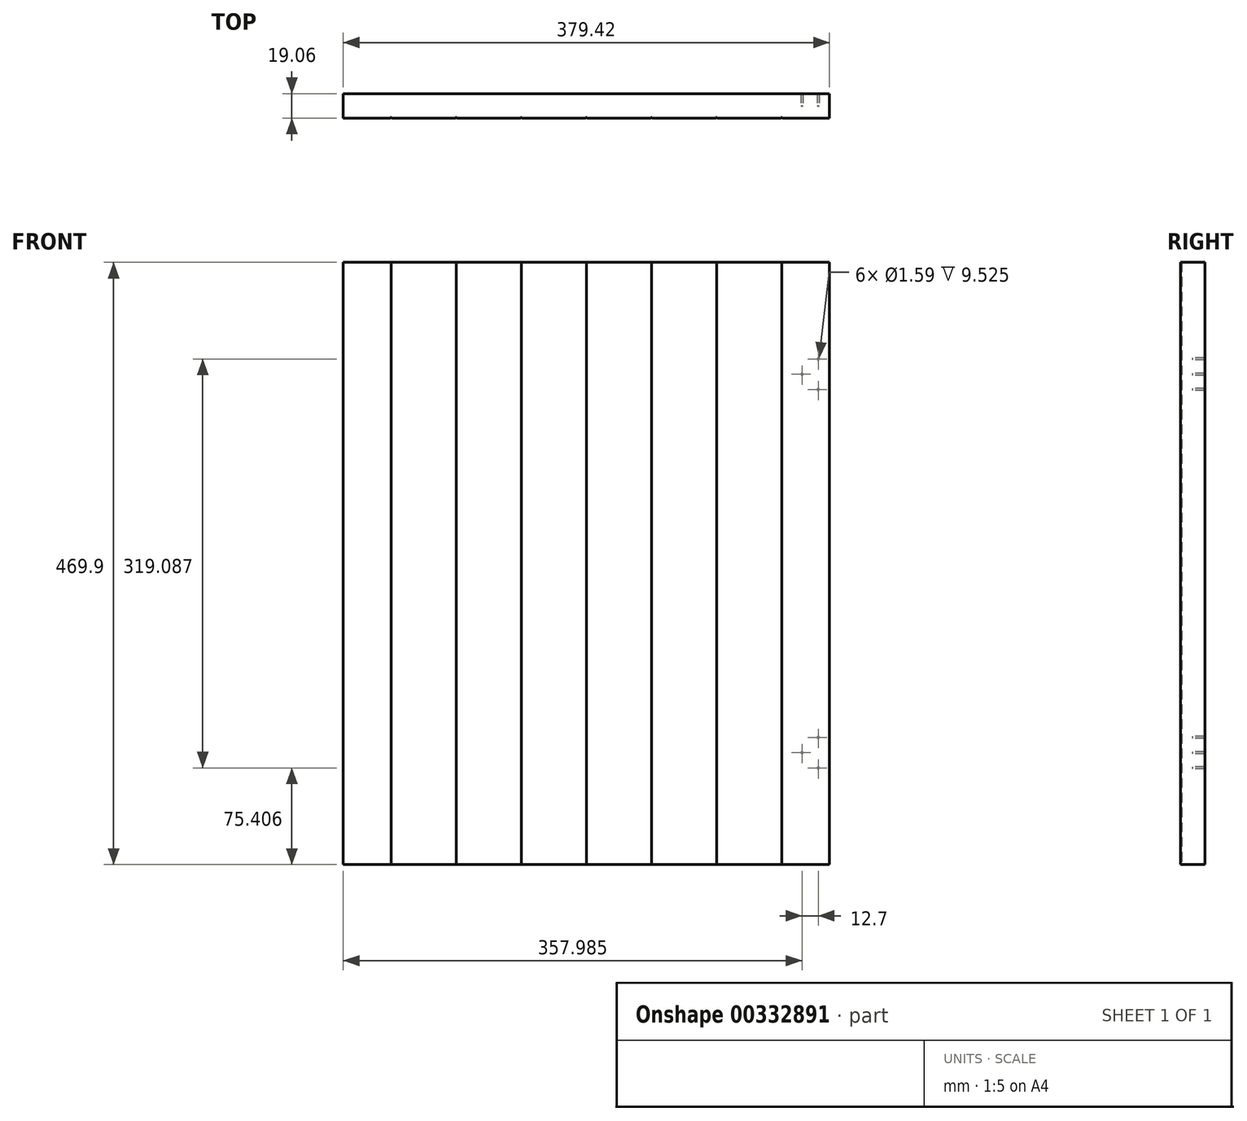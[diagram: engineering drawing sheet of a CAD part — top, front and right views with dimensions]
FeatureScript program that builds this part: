
annotation { "Feature Type Name" : "Feature", "Feature Type Description" : "" }
export const myFeature = defineFeature(function(context is Context, id is Id, definition is map)
    precondition{}
    {
        {
            var Q0;
            Q0=qCreatedBy(makeId("Top.planeOp"),FACE);
            var sketch = newSketch(context, id + "F0", { "sketchPlane" : qUnion([Q0])});
            skLineSegment(sketch, "E0.bottom", {"start": v(508, -9.53) * mm, "end": v(458.22, -9.53) * mm});
            skLineSegment(sketch, "E0.top", {"start": v(508, 9.53) * mm, "end": v(-508, 9.53) * mm});
            skLineSegment(sketch, "E0.left", {"start": v(508, 9.53) * mm, "end": v(508, -9.53) * mm});
            skLineSegment(sketch, "E0.right", {"start": v(-508, 9.53) * mm, "end": v(-508, -9.53) * mm});
            skPoint(sketch, "E0.middle", {"position": v(0, 0) * mm});
            skArc(sketch, "E1", {"start": v(-509.02, -9.53) * mm, "mid": v(-508.3, -9.23) * mm, "end": v(-508, -8.5) * mm});
            skArc(sketch, "E2", {"start": v(-508, -8.5) * mm, "mid": v(-507.7, -9.23) * mm, "end": v(-506.98, -9.52) * mm});
            skArc(sketch, "E3.1.0.0", {"start": v(-458.22, -9.53) * mm, "mid": v(-457.5, -9.23) * mm, "end": v(-457.2, -8.5) * mm});
            skArc(sketch, "E3.1.0.1", {"start": v(-457.2, -8.5) * mm, "mid": v(-456.9, -9.23) * mm, "end": v(-456.18, -9.52) * mm});
            skArc(sketch, "E3.2.0.0", {"start": v(-407.42, -9.53) * mm, "mid": v(-406.7, -9.23) * mm, "end": v(-406.4, -8.5) * mm});
            skArc(sketch, "E3.2.0.1", {"start": v(-406.4, -8.5) * mm, "mid": v(-406.1, -9.23) * mm, "end": v(-405.38, -9.52) * mm});
            skArc(sketch, "E3.3.0.0", {"start": v(-356.62, -9.53) * mm, "mid": v(-355.9, -9.23) * mm, "end": v(-355.6, -8.5) * mm});
            skArc(sketch, "E3.3.0.1", {"start": v(-355.6, -8.5) * mm, "mid": v(-355.3, -9.23) * mm, "end": v(-354.58, -9.52) * mm});
            skArc(sketch, "E3.4.0.0", {"start": v(-305.82, -9.53) * mm, "mid": v(-305.1, -9.23) * mm, "end": v(-304.8, -8.5) * mm});
            skArc(sketch, "E3.4.0.1", {"start": v(-304.8, -8.5) * mm, "mid": v(-304.5, -9.23) * mm, "end": v(-303.78, -9.52) * mm});
            skArc(sketch, "E3.5.0.0", {"start": v(-255.02, -9.53) * mm, "mid": v(-254.3, -9.23) * mm, "end": v(-254, -8.5) * mm});
            skArc(sketch, "E3.5.0.1", {"start": v(-254, -8.5) * mm, "mid": v(-253.7, -9.23) * mm, "end": v(-252.98, -9.52) * mm});
            skArc(sketch, "E3.6.0.0", {"start": v(-204.22, -9.53) * mm, "mid": v(-203.5, -9.23) * mm, "end": v(-203.2, -8.5) * mm});
            skArc(sketch, "E3.6.0.1", {"start": v(-203.2, -8.5) * mm, "mid": v(-202.9, -9.23) * mm, "end": v(-202.18, -9.52) * mm});
            skArc(sketch, "E3.7.0.0", {"start": v(-153.42, -9.53) * mm, "mid": v(-152.7, -9.23) * mm, "end": v(-152.4, -8.5) * mm});
            skArc(sketch, "E3.7.0.1", {"start": v(-152.4, -8.5) * mm, "mid": v(-152.1, -9.23) * mm, "end": v(-151.38, -9.52) * mm});
            skArc(sketch, "E3.8.0.0", {"start": v(-102.62, -9.53) * mm, "mid": v(-101.9, -9.23) * mm, "end": v(-101.6, -8.5) * mm});
            skArc(sketch, "E3.8.0.1", {"start": v(-101.6, -8.5) * mm, "mid": v(-101.3, -9.23) * mm, "end": v(-100.58, -9.52) * mm});
            skArc(sketch, "E3.9.0.0", {"start": v(-51.82, -9.53) * mm, "mid": v(-51.1, -9.23) * mm, "end": v(-50.8, -8.5) * mm});
            skArc(sketch, "E3.9.0.1", {"start": v(-50.8, -8.5) * mm, "mid": v(-50.5, -9.23) * mm, "end": v(-49.78, -9.52) * mm});
            skArc(sketch, "E3.10.0.0", {"start": v(-1.02, -9.53) * mm, "mid": v(-0.3, -9.23) * mm, "end": v(0, -8.5) * mm});
            skArc(sketch, "E3.10.0.1", {"start": v(0, -8.5) * mm, "mid": v(0.3, -9.23) * mm, "end": v(1.02, -9.52) * mm});
            skArc(sketch, "E3.11.0.0", {"start": v(49.78, -9.53) * mm, "mid": v(50.5, -9.23) * mm, "end": v(50.8, -8.5) * mm});
            skArc(sketch, "E3.11.0.1", {"start": v(50.8, -8.5) * mm, "mid": v(51.1, -9.23) * mm, "end": v(51.82, -9.52) * mm});
            skArc(sketch, "E3.12.0.0", {"start": v(100.58, -9.53) * mm, "mid": v(101.3, -9.23) * mm, "end": v(101.6, -8.5) * mm});
            skArc(sketch, "E3.12.0.1", {"start": v(101.6, -8.5) * mm, "mid": v(101.9, -9.23) * mm, "end": v(102.62, -9.52) * mm});
            skArc(sketch, "E3.13.0.0", {"start": v(151.38, -9.53) * mm, "mid": v(152.1, -9.23) * mm, "end": v(152.4, -8.5) * mm});
            skArc(sketch, "E3.13.0.1", {"start": v(152.4, -8.5) * mm, "mid": v(152.7, -9.23) * mm, "end": v(153.42, -9.52) * mm});
            skArc(sketch, "E3.14.0.0", {"start": v(202.18, -9.53) * mm, "mid": v(202.9, -9.23) * mm, "end": v(203.2, -8.5) * mm});
            skArc(sketch, "E3.14.0.1", {"start": v(203.2, -8.5) * mm, "mid": v(203.5, -9.23) * mm, "end": v(204.22, -9.52) * mm});
            skArc(sketch, "E3.15.0.0", {"start": v(252.98, -9.53) * mm, "mid": v(253.7, -9.23) * mm, "end": v(254, -8.5) * mm});
            skArc(sketch, "E3.15.0.1", {"start": v(254, -8.5) * mm, "mid": v(254.3, -9.23) * mm, "end": v(255.02, -9.52) * mm});
            skArc(sketch, "E3.16.0.0", {"start": v(303.78, -9.53) * mm, "mid": v(304.5, -9.23) * mm, "end": v(304.8, -8.5) * mm});
            skArc(sketch, "E3.16.0.1", {"start": v(304.8, -8.5) * mm, "mid": v(305.1, -9.23) * mm, "end": v(305.82, -9.52) * mm});
            skArc(sketch, "E3.17.0.0", {"start": v(354.58, -9.53) * mm, "mid": v(355.3, -9.23) * mm, "end": v(355.6, -8.5) * mm});
            skArc(sketch, "E3.17.0.1", {"start": v(355.6, -8.5) * mm, "mid": v(355.9, -9.23) * mm, "end": v(356.62, -9.52) * mm});
            skArc(sketch, "E3.18.0.0", {"start": v(405.38, -9.53) * mm, "mid": v(406.1, -9.23) * mm, "end": v(406.4, -8.5) * mm});
            skArc(sketch, "E3.18.0.1", {"start": v(406.4, -8.5) * mm, "mid": v(406.7, -9.23) * mm, "end": v(407.42, -9.52) * mm});
            skArc(sketch, "E3.19.0.0", {"start": v(456.18, -9.53) * mm, "mid": v(456.9, -9.23) * mm, "end": v(457.2, -8.5) * mm});
            skArc(sketch, "E3.19.0.1", {"start": v(457.2, -8.5) * mm, "mid": v(457.5, -9.23) * mm, "end": v(458.22, -9.52) * mm});
            skLineSegment(sketch, "E3.direction1", {"start": v(-506.98, -9.53) * mm, "end": v(-458.22, -9.53) * mm, "construction": true});
            skLineSegment(sketch, "E4.trimOffspring", {"start": v(-458.22, -9.53) * mm, "end": v(-508, -9.53) * mm});
            skLineSegment(sketch, "E5.trimOffspring", {"start": v(-407.42, -9.53) * mm, "end": v(-456.18, -9.53) * mm});
            skLineSegment(sketch, "E6.trimOffspring", {"start": v(-356.62, -9.53) * mm, "end": v(-405.38, -9.53) * mm});
            skLineSegment(sketch, "E7.trimOffspring", {"start": v(-305.82, -9.53) * mm, "end": v(-354.58, -9.53) * mm});
            skLineSegment(sketch, "E8.trimOffspring", {"start": v(-255.02, -9.53) * mm, "end": v(-303.78, -9.53) * mm});
            skLineSegment(sketch, "E9.trimOffspring", {"start": v(-204.22, -9.53) * mm, "end": v(-252.98, -9.53) * mm});
            skLineSegment(sketch, "E10.trimOffspring", {"start": v(-153.42, -9.53) * mm, "end": v(-202.18, -9.53) * mm});
            skLineSegment(sketch, "E11.trimOffspring", {"start": v(-102.62, -9.53) * mm, "end": v(-151.38, -9.53) * mm});
            skLineSegment(sketch, "E12.trimOffspring", {"start": v(-51.82, -9.53) * mm, "end": v(-100.58, -9.53) * mm});
            skLineSegment(sketch, "E13.trimOffspring", {"start": v(-1.02, -9.53) * mm, "end": v(-49.78, -9.53) * mm});
            skLineSegment(sketch, "E14.trimOffspring", {"start": v(49.78, -9.53) * mm, "end": v(1.02, -9.53) * mm});
            skLineSegment(sketch, "E15.trimOffspring", {"start": v(100.58, -9.53) * mm, "end": v(51.82, -9.53) * mm});
            skLineSegment(sketch, "E16.trimOffspring", {"start": v(151.38, -9.53) * mm, "end": v(102.62, -9.53) * mm});
            skLineSegment(sketch, "E17.trimOffspring", {"start": v(202.18, -9.53) * mm, "end": v(153.42, -9.53) * mm});
            skLineSegment(sketch, "E18.trimOffspring", {"start": v(252.98, -9.53) * mm, "end": v(204.22, -9.53) * mm});
            skLineSegment(sketch, "E19.trimOffspring", {"start": v(303.78, -9.53) * mm, "end": v(255.02, -9.53) * mm});
            skLineSegment(sketch, "E20.trimOffspring", {"start": v(354.58, -9.53) * mm, "end": v(305.82, -9.53) * mm});
            skLineSegment(sketch, "E21.trimOffspring", {"start": v(405.38, -9.53) * mm, "end": v(356.62, -9.53) * mm});
            skLineSegment(sketch, "E22.trimOffspring", {"start": v(456.18, -9.53) * mm, "end": v(407.42, -9.53) * mm});
            skSolve(sketch);
        }
        {
            var Q0;
            Q0=qSketchRegion(id+"F0",true);
            extrude(context, id + "F1", {"entities" : qUnion([Q0]), "depth" : 469.9 * mm});
        }
        {
            var Q0;
            Q0=qCreatedBy(makeId("Top.planeOp"),FACE);
            var sketch = newSketch(context, id + "F2", { "sketchPlane" : qUnion([Q0])});
            skLineSegment(sketch, "E23.bottom", {"start": v(189.7, -89.59) * mm, "end": v(532.78, -89.59) * mm});
            skLineSegment(sketch, "E23.top", {"start": v(189.7, 47.64) * mm, "end": v(532.78, 47.64) * mm});
            skLineSegment(sketch, "E23.left", {"start": v(189.7, -89.59) * mm, "end": v(189.7, 47.64) * mm});
            skLineSegment(sketch, "E23.right", {"start": v(532.78, -89.59) * mm, "end": v(532.78, 47.64) * mm});
            skLineSegment(sketch, "E24.bottom", {"start": v(-189.7, -137.09) * mm, "end": v(-570.7, -137.09) * mm});
            skLineSegment(sketch, "E24.top", {"start": v(-189.7, 58.2) * mm, "end": v(-570.7, 58.2) * mm});
            skLineSegment(sketch, "E24.left", {"start": v(-189.7, -137.09) * mm, "end": v(-189.7, 58.2) * mm});
            skLineSegment(sketch, "E24.right", {"start": v(-570.7, -137.09) * mm, "end": v(-570.7, 58.2) * mm});
            skSolve(sketch);
        }
        {
            var Q0;
            Q0=qSketchRegion(id+"F2",true);
            extrude(context, id + "F3", {"entities" : qUnion([Q0]), "operationType" : NewBodyOperationType.REMOVE, "depth" : 1143 * mm});
        }
        {
            var Q0;
            Q0=qCreatedBy(makeId("Front.planeOp"),FACE);
            var sketch = newSketch(context, id + "F4", { "sketchPlane" : qUnion([Q0])});
            skPoint(sketch, "E25.middle", {"position": v(0, 454.03) * mm});
            skLineSegment(sketch, "E26.bottom", {"start": v(168.28, 0) * mm, "end": v(180.98, 0) * mm, "construction": true});
            skLineSegment(sketch, "E26.top", {"start": v(168.28, 469.9) * mm, "end": v(180.97, 469.9) * mm, "construction": true});
            skLineSegment(sketch, "E26.left", {"start": v(168.28, 0) * mm, "end": v(168.27, 394.5) * mm, "construction": true});
            skLineSegment(sketch, "E26.right", {"start": v(180.98, 0) * mm, "end": v(180.97, 469.9) * mm, "construction": true});
            skLineSegment(sketch, "E27", {"start": v(168.27, 382.59) * mm, "end": v(167.48, 382.59) * mm, "construction": true});
            skLineSegment(sketch, "E28", {"start": v(168.28, 87.31) * mm, "end": v(-344.18, 87.31) * mm, "construction": true});
            skLineSegment(sketch, "E29", {"start": v(180.97, 394.5) * mm, "end": v(168.27, 394.5) * mm, "construction": true});
            skLineSegment(sketch, "E30", {"start": v(168.27, 370.68) * mm, "end": v(180.97, 370.68) * mm, "construction": true});
            skLineSegment(sketch, "E31", {"start": v(-420, 75.4) * mm, "end": v(180.97, 75.4) * mm, "construction": true});
            skLineSegment(sketch, "E32", {"start": v(180.97, 99.22) * mm, "end": v(-422.85, 99.22) * mm, "construction": true});
            skCircle(sketch, "E33", {"center": v(180.97, 394.5) * mm, "radius": 0.8 * mm});
            skCircle(sketch, "E34", {"center": v(168.27, 382.59) * mm, "radius": 0.8 * mm});
            skCircle(sketch, "E35", {"center": v(180.97, 370.68) * mm, "radius": 0.8 * mm});
            skCircle(sketch, "E36", {"center": v(180.97, 99.22) * mm, "radius": 0.8 * mm});
            skCircle(sketch, "E37", {"center": v(168.28, 87.31) * mm, "radius": 0.8 * mm});
            skCircle(sketch, "E38", {"center": v(180.97, 75.4) * mm, "radius": 0.8 * mm});
            skPoint(sketch, "E39.orphan", {"position": v(-190.5, 482.31) * mm});
            skPoint(sketch, "E40.orphan", {"position": v(-190.5, 425.74) * mm});
            skPoint(sketch, "E41.center.orphan", {"position": v(-115.1, 454.03) * mm});
            skPoint(sketch, "E42.orphan", {"position": v(-423.07, 394.5) * mm});
            skPoint(sketch, "E43.orphan", {"position": v(-423.07, 370.68) * mm});
            skPoint(sketch, "E44.orphan", {"position": v(190.5, 482.31) * mm});
            skPoint(sketch, "E25.left.end.orphan", {"position": v(190.5, 425.74) * mm});
            skSolve(sketch);
        }
        {
            var Q0;
            Q0=qSketchRegion(id+"F4",true);
            extrude(context, id + "F5", {"entities" : qUnion([Q0]), "operationType" : NewBodyOperationType.REMOVE, "oppositeDirection" : true, "depth" : 25.4 * mm});
        }
    });
